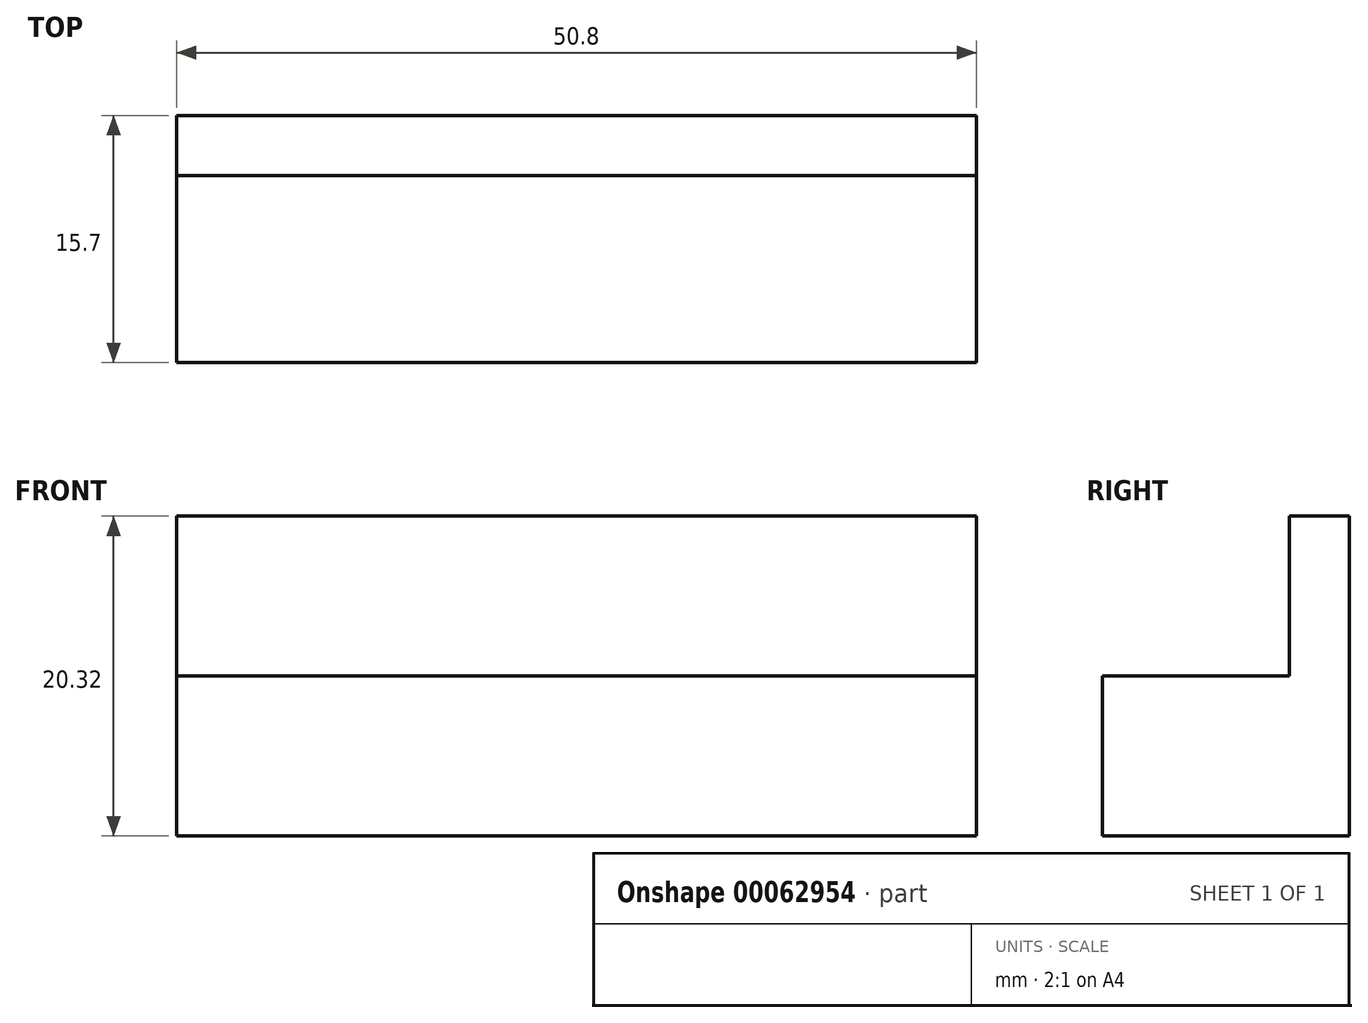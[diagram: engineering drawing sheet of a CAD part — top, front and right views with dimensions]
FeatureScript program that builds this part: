
annotation { "Feature Type Name" : "Feature", "Feature Type Description" : "" }
export const myFeature = defineFeature(function(context is Context, id is Id, definition is map)
    precondition{}
    {
        {
            var Q0;
            Q0=qCreatedBy(makeId("Top.planeOp"),FACE);
            var sketch = newSketch(context, id + "F0", { "sketchPlane" : qUnion([Q0])});
            skLineSegment(sketch, "E0.rect.top", {"start": v(-25.4, 6.35) * mm, "end": v(25.4, 6.35) * mm});
            skLineSegment(sketch, "E0.rect.left", {"start": v(-25.4, -6.35) * mm, "end": v(-25.4, 6.35) * mm});
            skLineSegment(sketch, "E0.rect.right", {"start": v(25.4, -6.35) * mm, "end": v(25.4, 6.35) * mm});
            skPoint(sketch, "E0.rect.middle", {"position": v(0, 0) * mm});
            skLineSegment(sketch, "E1.bottom", {"start": v(-25.4, -9.35) * mm, "end": v(25.4, -9.35) * mm});
            skLineSegment(sketch, "E1.left", {"start": v(-25.4, -9.35) * mm, "end": v(-25.4, -6.35) * mm});
            skLineSegment(sketch, "E1.right", {"start": v(25.4, -9.35) * mm, "end": v(25.4, -6.35) * mm});
            skSolve(sketch);
        }
        {
            var Q0;
            Q0 = qSketchRegion(id + "F0", true);
            extrude(context, id + "F1", {"entities" : qUnion([Q0]), "depth" : 10.16 * mm});
        }
        {
            var Q0;
            Q0=makeQuery(id+"F1.opExtrude","CAP_FACE",FACE,{"disambiguationData":[OSD([sQuery(id+"F0.wireOp",EDGE,"E0.rect.bottom"),sQuery(id+"F0.wireOp",EDGE,"E0.rect.top"),sQuery(id+"F0.wireOp",EDGE,"E0.rect.left"),sQuery(id+"F0.wireOp",EDGE,"E0.rect.right")])],"isStart":false});
            var sketch = newSketch(context, id + "F2", { "sketchPlane" : qUnion([Q0])});
            skLineSegment(sketch, "E2.bottom", {"start": v(-25.4, 6.35) * mm, "end": v(25.4, 6.35) * mm});
            skLineSegment(sketch, "E2.top", {"start": v(-25.4, 2.54) * mm, "end": v(25.4, 2.54) * mm});
            skLineSegment(sketch, "E2.left", {"start": v(-25.4, 6.35) * mm, "end": v(-25.4, 2.54) * mm});
            skLineSegment(sketch, "E2.right", {"start": v(25.4, 6.35) * mm, "end": v(25.4, 2.54) * mm});
            skSolve(sketch);
        }
        {
            var Q0;
            Q0 = qSketchRegion(id + "F2", true);
            extrude(context, id + "F3", {"entities" : qUnion([Q0]), "operationType" : NewBodyOperationType.ADD, "depth" : 10.16 * mm});
        }
    });
